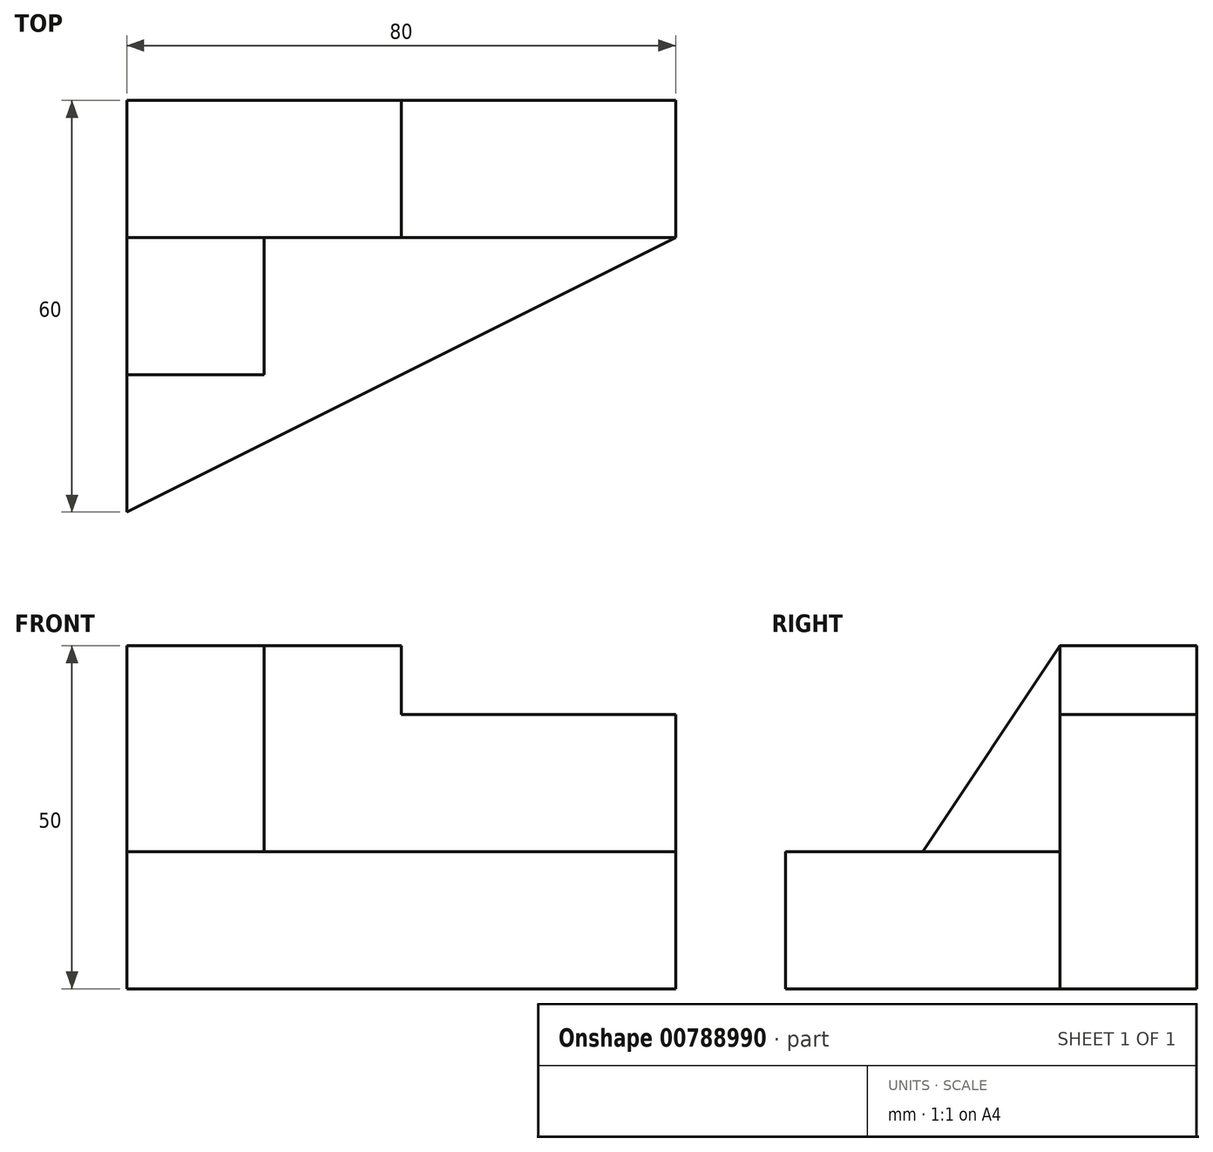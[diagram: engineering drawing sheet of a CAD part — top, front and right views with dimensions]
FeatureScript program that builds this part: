
annotation { "Feature Type Name" : "Feature", "Feature Type Description" : "" }
export const myFeature = defineFeature(function(context is Context, id is Id, definition is map)
    precondition{}
    {
        {
            var Q0;
            Q0=qCreatedBy(makeId("Top.planeOp"),FACE);
            var sketch = newSketch(context, id + "F0", { "sketchPlane" : qUnion([Q0])});
            skLineSegment(sketch, "E0", {"start": v(0, 0) * mm, "end": v(80, 0) * mm});
            skLineSegment(sketch, "E1", {"start": v(80, 0) * mm, "end": v(80, -20) * mm});
            skLineSegment(sketch, "E2", {"start": v(80, -20) * mm, "end": v(0, -60) * mm});
            skLineSegment(sketch, "E3", {"start": v(0, -60) * mm, "end": v(0, 0) * mm});
            skSolve(sketch);
        }
        {
            var Q0;
            Q0=makeQuery(id+"F0.imprint","IMPRINT",FACE,{"disambiguationData":[TD([[makeQuery(id+"F0.imprint","IMPRINT",EDGE,{"derivedFrom":sQuery(id+"F0.wireOp",EDGE,"E0")}),-1.0]])]});
            extrude(context, id + "F1", {"entities" : qUnion([Q0]), "depth" : 20 * mm, "offsetDistance" : 25 * mm});
        }
        {
            var Q0;
            Q0=makeQuery(id+"F1.opExtrude","CAP_FACE",FACE,{"disambiguationData":[OSD([sQuery(id+"F0.wireOp",EDGE,"E0"),sQuery(id+"F0.wireOp",EDGE,"E1"),sQuery(id+"F0.wireOp",EDGE,"E2"),sQuery(id+"F0.wireOp",EDGE,"E3")])],"isStart":false});
            var sketch = newSketch(context, id + "F2", { "sketchPlane" : qUnion([Q0])});
            skLineSegment(sketch, "E4.bottom", {"start": v(0, 0) * mm, "end": v(40, 0) * mm});
            skLineSegment(sketch, "E4.top", {"start": v(0, -20) * mm, "end": v(40, -20) * mm});
            skLineSegment(sketch, "E4.left", {"start": v(0, 0) * mm, "end": v(0, -20) * mm});
            skLineSegment(sketch, "E4.right", {"start": v(40, 0) * mm, "end": v(40, -20) * mm});
            skLineSegment(sketch, "E5.bottom", {"start": v(40, -20) * mm, "end": v(80, -20) * mm});
            skLineSegment(sketch, "E5.top", {"start": v(40, 0) * mm, "end": v(80, 0) * mm});
            skLineSegment(sketch, "E5.left", {"start": v(40, -20) * mm, "end": v(40, 0) * mm});
            skLineSegment(sketch, "E5.right", {"start": v(80, -20) * mm, "end": v(80, 0) * mm});
            skSolve(sketch);
        }
        {
            var Q0;
            Q0=makeQuery(id+"F2.imprint","IMPRINT",FACE,{"disambiguationData":[TD([[makeQuery(id+"F2.imprint","IMPRINT",EDGE,{"derivedFrom":sQuery(id+"F2.wireOp",EDGE,"E4.bottom")}),-1.0]])]});
            extrude(context, id + "F3", {"entities" : qUnion([Q0]), "operationType" : NewBodyOperationType.ADD, "depth" : 30 * mm, "offsetDistance" : 25 * mm});
        }
        {
            var Q0;
            Q0=makeQuery(id+"F2.imprint","IMPRINT",FACE,{"disambiguationData":[TD([[makeQuery(id+"F2.imprint","IMPRINT",EDGE,{"derivedFrom":sQuery(id+"F2.wireOp",EDGE,"E5.bottom")}),1.0]])]});
            extrude(context, id + "F4", {"entities" : qUnion([Q0]), "operationType" : NewBodyOperationType.ADD, "depth" : 20 * mm, "offsetDistance" : 25 * mm});
        }
        {
            var Q0;
            Q0=makeQuery(id+"F3.boolean.opBoolean","MERGE",FACE,{"derivedFrom":[makeQuery(id+"F1.opExtrude","SWEPT_FACE",FACE,{"disambiguationData":[OSD([sQuery(id+"F0.wireOp",EDGE,"E3")])]}),makeQuery(id+"F3.opExtrude","SWEPT_FACE",FACE,{"disambiguationData":[OSD([sQuery(id+"F2.wireOp",EDGE,"E4.left")])]})]});
            var sketch = newSketch(context, id + "F5", { "sketchPlane" : qUnion([Q0])});
            skLineSegment(sketch, "E6", {"start": v(20, 50) * mm, "end": v(20, 20) * mm});
            skLineSegment(sketch, "E7", {"start": v(20, 20) * mm, "end": v(40, 20) * mm});
            skLineSegment(sketch, "E8", {"start": v(40, 20) * mm, "end": v(20, 50) * mm});
            skSolve(sketch);
        }
        {
            var Q0;
            Q0=makeQuery(id+"F5.imprint","IMPRINT",FACE,{"disambiguationData":[TD([[makeQuery(id+"F5.imprint","IMPRINT",EDGE,{"derivedFrom":sQuery(id+"F5.wireOp",EDGE,"E6")}),1.0]])]});
            extrude(context, id + "F6", {"entities" : qUnion([Q0]), "operationType" : NewBodyOperationType.ADD, "oppositeDirection" : true, "depth" : 20 * mm, "offsetDistance" : 25 * mm});
        }
    });
